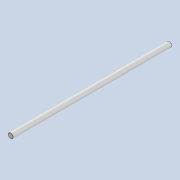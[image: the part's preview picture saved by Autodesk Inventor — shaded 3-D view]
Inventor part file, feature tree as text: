
AUTODESK INVENTOR PART (.ipt)
format: ipt  version: 2020 (Build 240168000, 168)  size: 87,040 bytes
history: native  units: mm
features: extrude x1, chamfer x1, sketch x1
ambient origin geometry x8: Origin, YZ Plane, XZ Plane, XY Plane, X Axis, Y Axis, Z Axis, Center Point
bodies: Solid1 (feature_tree)
feature tree (3):
  extrude  "Extrusion1"  Depth=352.0mm TaperAngle=0.0deg
  chamfer  "Chamfer1"  Distance=0.5mm Angle=45.0deg
  sketch  "Sketch1"  dims[d0=10.0mm d1=352.0mm d2=0.0mm d3=0.5mm d4=2.0mm d5=45.0deg]
